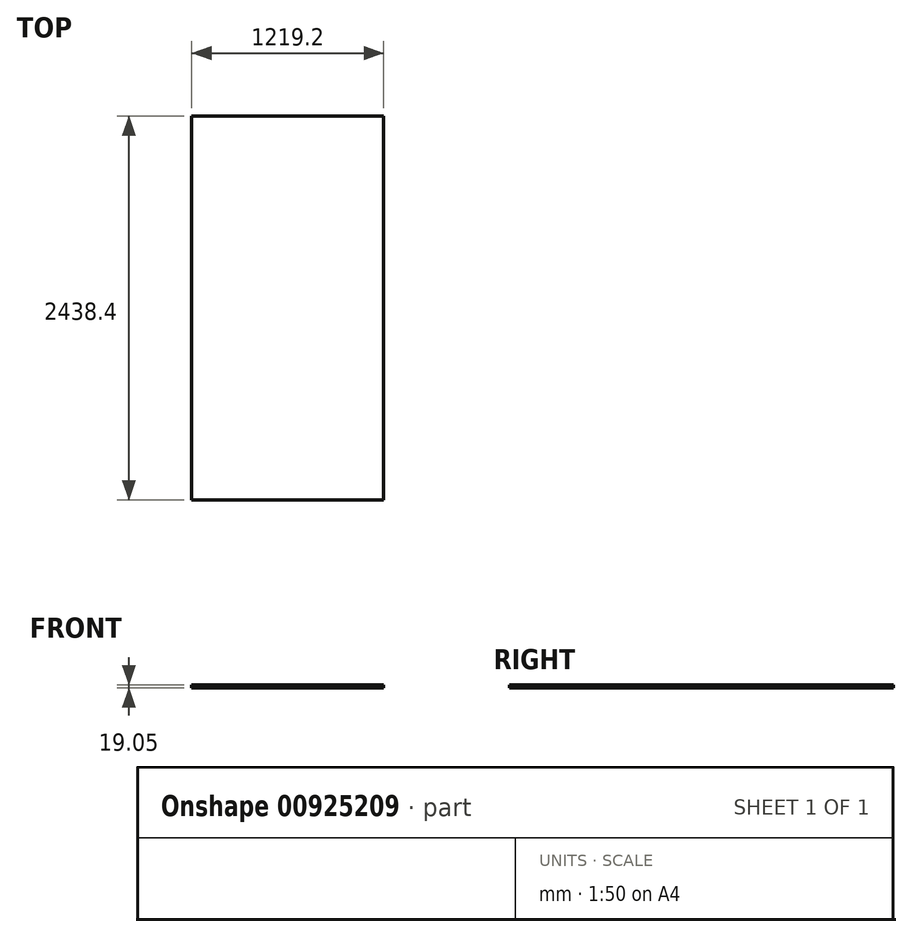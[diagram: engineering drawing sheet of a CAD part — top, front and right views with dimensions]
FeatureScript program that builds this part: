
annotation { "Feature Type Name" : "Feature", "Feature Type Description" : "" }
export const myFeature = defineFeature(function(context is Context, id is Id, definition is map)
    precondition{}
    {
        {
            var Q0;
            Q0=qCreatedBy(makeId("Top.planeOp"),FACE);
            var sketch = newSketch(context, id + "F0", { "sketchPlane" : qUnion([Q0])});
            skLineSegment(sketch, "E0.bottom", {"start": v(0, 0) * mm, "end": v(1219.2, 0) * mm});
            skLineSegment(sketch, "E0.top", {"start": v(0, 2438.4) * mm, "end": v(1219.2, 2438.4) * mm});
            skLineSegment(sketch, "E0.left", {"start": v(0, 0) * mm, "end": v(0, 2438.4) * mm});
            skLineSegment(sketch, "E0.right", {"start": v(1219.2, 0) * mm, "end": v(1219.2, 2438.4) * mm});
            skSolve(sketch);
        }
        {
            var Q0;
            Q0 = qSketchRegion(id + "F0", true);
            extrude(context, id + "F1", {"entities" : qUnion([Q0]), "depth" : 19.05 * mm, "offsetDistance" : 25.4 * mm});
        }
    });
